# Revit family: LB Ledge
name_source: partatom
category: Furniture
units: mm (PartAtom-declared; Revit-internal decimal feet)

## family parameters
Always vertical = Yes
Cut with Voids When Loaded = No
OmniClass Number = 23.40.20.00
OmniClass Title = General Furniture and Specialties
Room Calculation Point = No
Shared = No
Work Plane-Based = No

## types (10) — shared parameters
Default Elevation = 0' - 0"
Height = 2' - 10"
Manufacturer = AIS Inc
Product = LB LEDGE
URL = https://www.ais-inc.com

## per-type parameters (varying)
| type | Description |
| F-LBLL1348 | 48Wx13D LB Ledge |
| F-LBLL1354 | 54Wx13D LB Ledge |
| F-LBLL1360 | 60Wx13D LB Ledge |
| F-LBLL1366 | 66Wx13D LB Ledge |
| F-LBLL1372 | 72Wx13D LB Ledge |
| F-LBLL1548 | 48Wx15D LB Ledge |
| F-LBLL1554 | 54Wx15D LB Ledge |
| F-LBLL1560 | 60Wx15D LB Ledge |
| F-LBLL1566 | 66Wx15D LB Ledge |
| F-LBLL1572 | 72Wx15D LB Ledge |

note: column(s) folded — value = type name in every type: Model

type visibility flags: 10 boolean params named "<type name>" — each type sets only its own to Yes (folded from table)

## geometry (parser evidence)
native form markers: Sweep x3
no freeform markers — native parametric forms only
